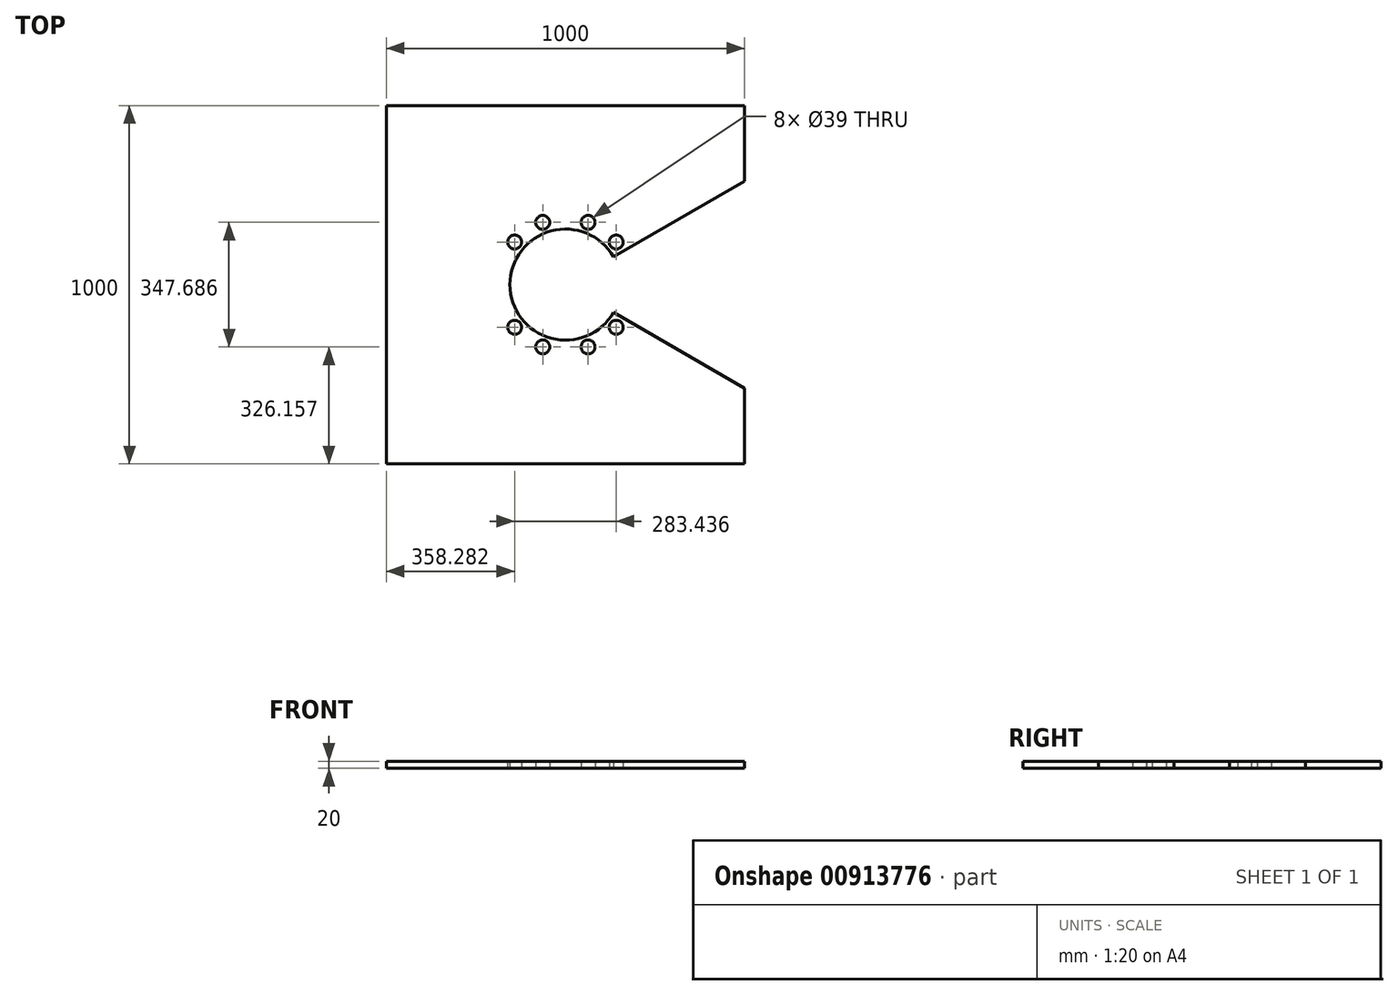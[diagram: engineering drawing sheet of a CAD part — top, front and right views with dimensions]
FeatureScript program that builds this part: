
annotation { "Feature Type Name" : "Feature", "Feature Type Description" : "" }
export const myFeature = defineFeature(function(context is Context, id is Id, definition is map)
    precondition{}
    {
        {
            var Q0;
            Q0=qCreatedBy(makeId("Top.planeOp"),FACE);
            var sketch = newSketch(context, id + "F0", { "sketchPlane" : qUnion([Q0])});
            skCircle(sketch, "E0", {"center": v(0, 0) * mm, "radius": 185 * mm, "construction": true});
            skLineSegment(sketch, "E1", {"start": v(0, 0) * mm, "end": v(72.3, 198.65) * mm, "construction": true});
            skCircle(sketch, "E2", {"center": v(63.27, 173.84) * mm, "radius": 19.5 * mm});
            skLineSegment(sketch, "E3", {"start": v(0, 0) * mm, "end": v(150.95, 126.66) * mm, "construction": true});
            skLineSegment(sketch, "E4", {"start": v(0, 0) * mm, "end": v(-63.14, 173.48) * mm, "construction": true});
            skLineSegment(sketch, "E5", {"start": v(0, 0) * mm, "end": v(-153.87, 129.1) * mm, "construction": true});
            skCircle(sketch, "E6", {"center": v(-63.27, 173.84) * mm, "radius": 19.5 * mm});
            skCircle(sketch, "E7", {"center": v(-141.72, 118.92) * mm, "radius": 19.5 * mm});
            skCircle(sketch, "E8", {"center": v(141.72, 118.92) * mm, "radius": 19.5 * mm});
            skCircle(sketch, "E9.MirrorC", {"center": v(-141.72, -118.92) * mm, "radius": 19.5 * mm});
            skCircle(sketch, "E10.MirrorC", {"center": v(-63.27, -173.84) * mm, "radius": 19.5 * mm});
            skCircle(sketch, "E11.MirrorC", {"center": v(63.27, -173.84) * mm, "radius": 19.5 * mm});
            skCircle(sketch, "E12.MirrorC", {"center": v(141.72, -118.92) * mm, "radius": 19.5 * mm});
            skArc(sketch, "E13", {"start": v(195.77, 88.87) * mm, "mid": v(-215, -0.82) * mm, "end": v(196.45, -87.36) * mm, "construction": true});
            skArc(sketch, "E14", {"start": v(128.03, 87.36) * mm, "mid": v(-155, 0) * mm, "end": v(128.03, -87.36) * mm});
            skCircle(sketch, "E15", {"center": v(0, 0) * mm, "radius": 77.5 * mm, "construction": true});
            skArc(sketch, "E16", {"start": v(128.03, 87.36) * mm, "mid": v(131.23, 82.5) * mm, "end": v(134.23, 77.5) * mm});
            skArc(sketch, "E17", {"start": v(195.77, 88.87) * mm, "mid": v(198.24, 83.22) * mm, "end": v(200.55, 77.5) * mm});
            skArc(sketch, "E18.trimOffspring", {"start": v(200.55, -77.5) * mm, "mid": v(198.56, -82.46) * mm, "end": v(196.45, -87.36) * mm});
            skArc(sketch, "E19.trimOffspring", {"start": v(134.23, -77.5) * mm, "mid": v(131.23, -82.5) * mm, "end": v(128.03, -87.36) * mm});
            skLineSegment(sketch, "E20.bottom", {"start": v(-500, 500) * mm, "end": v(500, 500) * mm});
            skLineSegment(sketch, "E20.top", {"start": v(-500, -500) * mm, "end": v(500, -500) * mm});
            skLineSegment(sketch, "E20.left", {"start": v(-500, 500) * mm, "end": v(-500, -500) * mm});
            skLineSegment(sketch, "E20.right", {"start": v(500, 500) * mm, "end": v(500, 77.5) * mm});
            skLineSegment(sketch, "E21.bottom", {"start": v(500, 77.5) * mm, "end": v(134.23, 77.5) * mm});
            skLineSegment(sketch, "E21.top", {"start": v(500, -77.5) * mm, "end": v(134.23, -77.5) * mm});
            skLineSegment(sketch, "E22.trimOffspring", {"start": v(500, -77.5) * mm, "end": v(500, -500) * mm});
            skLineSegment(sketch, "E23", {"start": v(0, 0) * mm, "end": v(669.45, 386.5) * mm});
            skLineSegment(sketch, "E24.MirrorCS", {"start": v(0, 0) * mm, "end": v(669.45, -386.5) * mm});
            skSolve(sketch);
        }
        {
            var Q0;
            Q0=makeQuery(id+"F0.imprint","IMPRINT",FACE,{"disambiguationData":[TD([[makeQuery(id+"F0.imprint","IMPRINT",EDGE,{"derivedFrom":sQuery(id+"F0.wireOp",EDGE,"E2")}),-1.0]])]});
            extrude(context, id + "F1", {"entities" : qUnion([Q0]), "depth" : 20 * mm, "offsetDistance" : 25 * mm});
        }
    });
